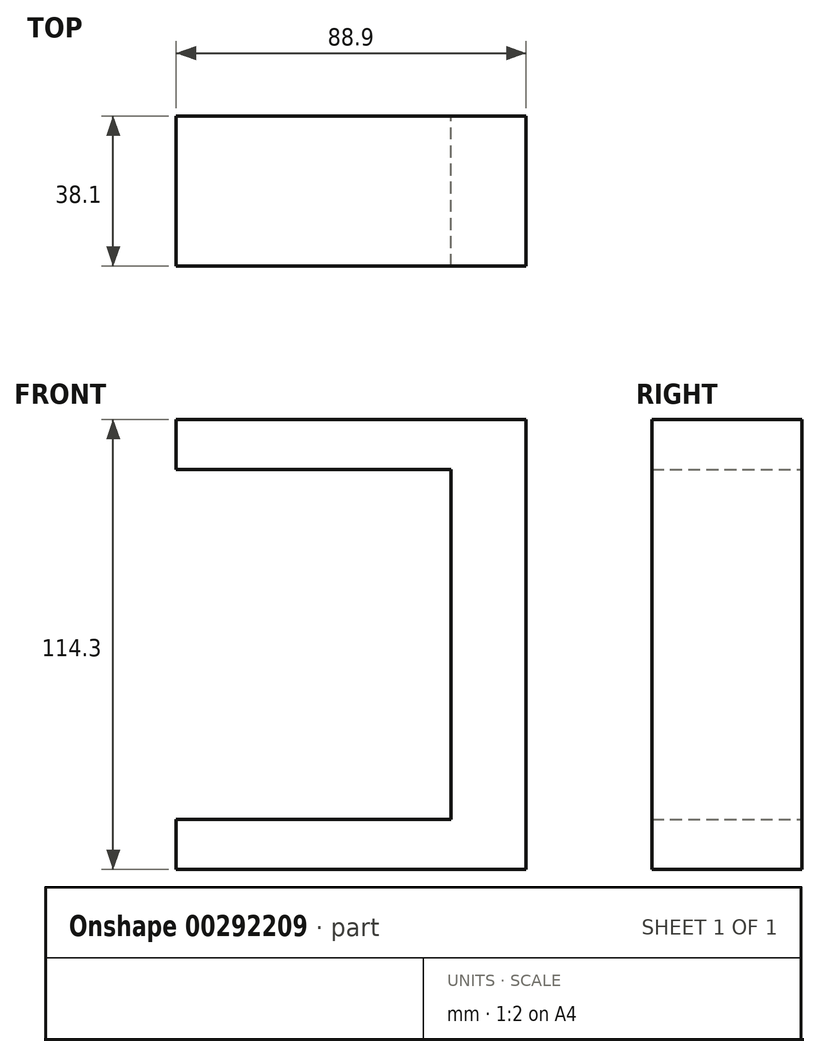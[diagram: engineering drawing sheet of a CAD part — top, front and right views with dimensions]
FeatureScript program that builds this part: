
annotation { "Feature Type Name" : "Feature", "Feature Type Description" : "" }
export const myFeature = defineFeature(function(context is Context, id is Id, definition is map)
    precondition{}
    {
        {
            var Q0;
            Q0=qCreatedBy(makeId("Front.planeOp"),FACE);
            var sketch = newSketch(context, id + "F0", { "sketchPlane" : qUnion([Q0])});
            skLineSegment(sketch, "E0", {"start": v(0, 0) * mm, "end": v(0, 114.3) * mm});
            skLineSegment(sketch, "E1", {"start": v(0, 114.3) * mm, "end": v(-88.9, 114.3) * mm});
            skLineSegment(sketch, "E2", {"start": v(-88.9, 114.3) * mm, "end": v(-88.9, 101.6) * mm});
            skLineSegment(sketch, "E3", {"start": v(-88.9, 101.6) * mm, "end": v(-19.05, 101.6) * mm});
            skLineSegment(sketch, "E4", {"start": v(0, 0) * mm, "end": v(-88.9, 0) * mm});
            skLineSegment(sketch, "E5", {"start": v(-88.9, 0) * mm, "end": v(-88.9, 12.7) * mm});
            skLineSegment(sketch, "E6", {"start": v(-88.9, 12.7) * mm, "end": v(-19.05, 12.7) * mm});
            skLineSegment(sketch, "E7", {"start": v(-19.05, 12.7) * mm, "end": v(-19.05, 101.6) * mm});
            skSolve(sketch);
        }
        {
            var Q0;
            Q0=makeQuery(id+"F0.imprint","IMPRINT",FACE,{"disambiguationData":[TD([[makeQuery(id+"F0.imprint","IMPRINT",EDGE,{"derivedFrom":sQuery(id+"F0.wireOp",EDGE,"E0")}),1.0]])]});
            extrude(context, id + "F1", {"entities" : qUnion([Q0]), "depth" : 38.1 * mm});
        }
    });
